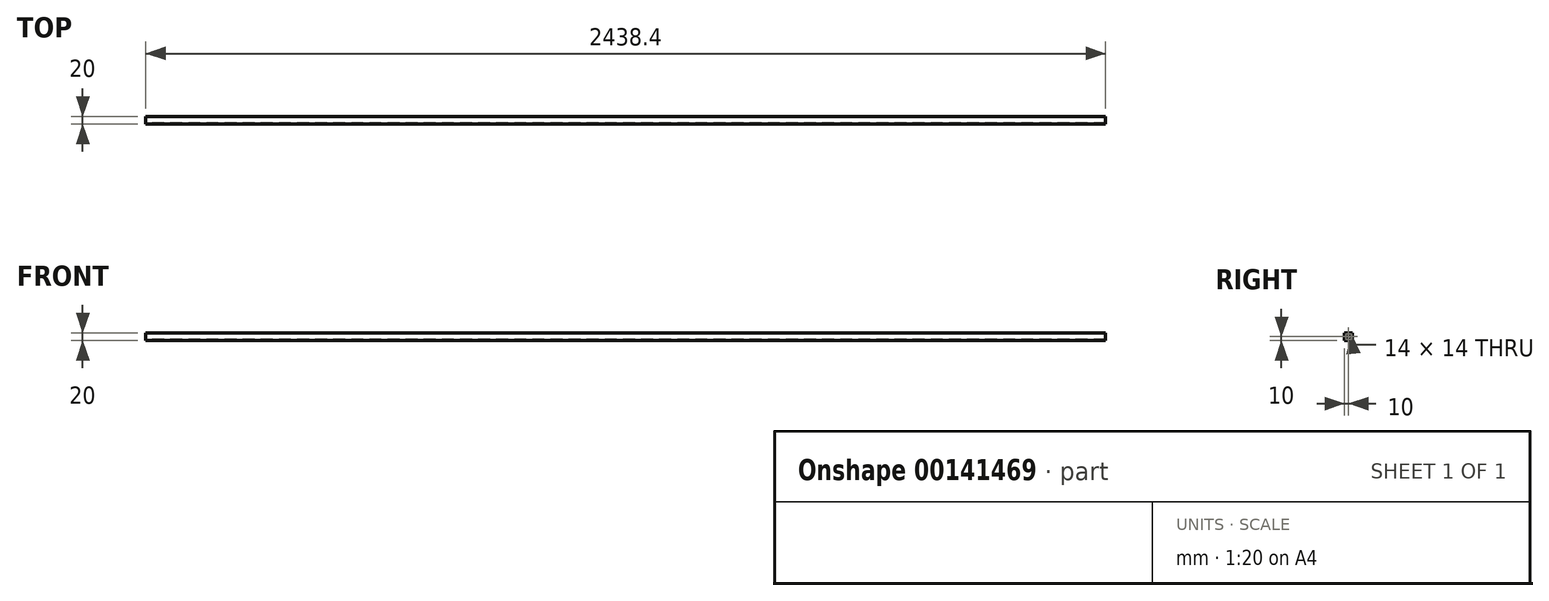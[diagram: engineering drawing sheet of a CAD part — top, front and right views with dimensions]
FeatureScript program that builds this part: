
annotation { "Feature Type Name" : "Feature", "Feature Type Description" : "" }
export const myFeature = defineFeature(function(context is Context, id is Id, definition is map)
    precondition{}
    {
        {
            var Q0;
            Q0=qCreatedBy(makeId("Right.planeOp"),FACE);
            var sketch = newSketch(context, id + "F0", { "sketchPlane" : qUnion([Q0])});
            skLineSegment(sketch, "E0.bottom", {"start": v(-10, -10) * mm, "end": v(10, -10) * mm});
            skLineSegment(sketch, "E0.top", {"start": v(-10, 10) * mm, "end": v(10, 10) * mm});
            skLineSegment(sketch, "E0.left", {"start": v(-10, -10) * mm, "end": v(-10, 10) * mm});
            skLineSegment(sketch, "E0.right", {"start": v(10, -10) * mm, "end": v(10, 10) * mm});
            skPoint(sketch, "E0.middle", {"position": v(0, 0) * mm});
            skLineSegment(sketch, "E1.0", {"start": v(-7, 7) * mm, "end": v(7, 7) * mm});
            skLineSegment(sketch, "E1.1", {"start": v(-7, -7) * mm, "end": v(-7, 7) * mm});
            skLineSegment(sketch, "E1.2", {"start": v(-7, -7) * mm, "end": v(7, -7) * mm});
            skLineSegment(sketch, "E1.3", {"start": v(7, -7) * mm, "end": v(7, 7) * mm});
            skSolve(sketch);
        }
        {
            var Q0;
            Q0 = qSketchRegion(id + "F0", true);
            extrude(context, id + "F1", {"entities" : qUnion([Q0]), "depth" : 2438.4 * mm});
        }
    });
